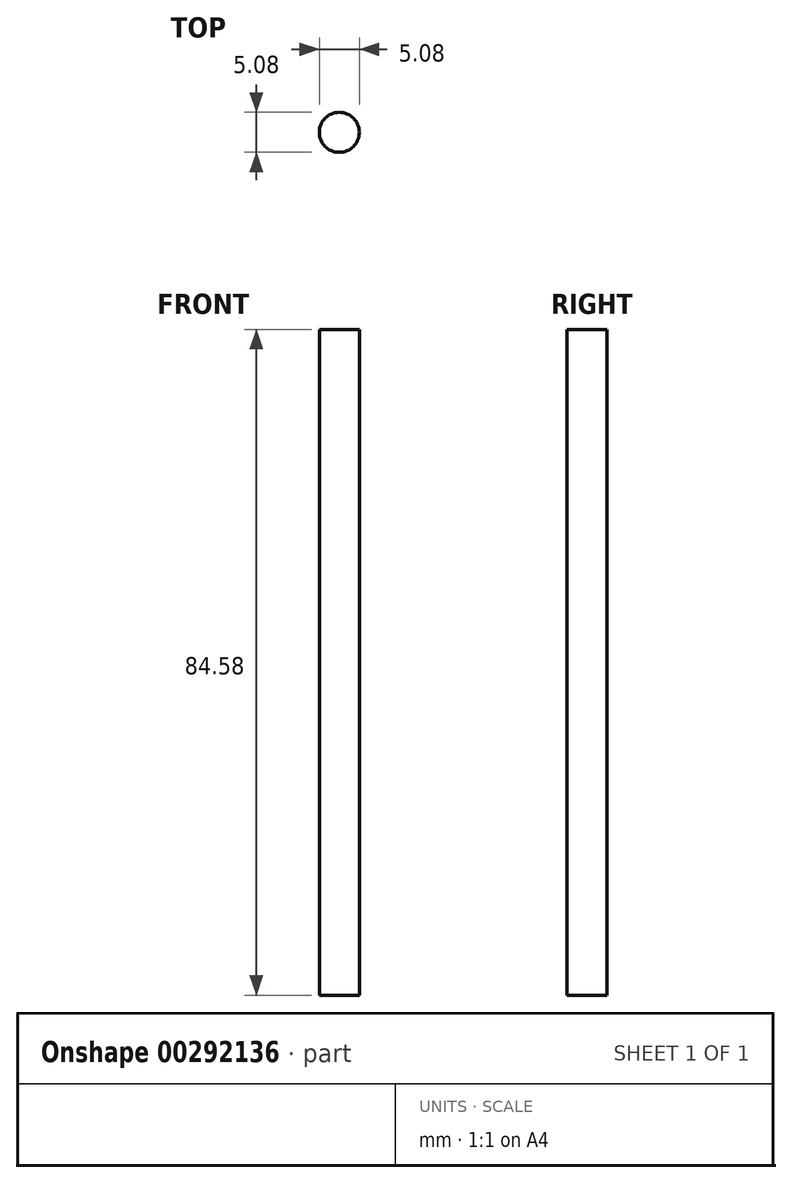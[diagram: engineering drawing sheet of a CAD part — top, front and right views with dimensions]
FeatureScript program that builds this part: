
annotation { "Feature Type Name" : "Feature", "Feature Type Description" : "" }
export const myFeature = defineFeature(function(context is Context, id is Id, definition is map)
    precondition{}
    {
        {
            var Q0;
            Q0=qCreatedBy(makeId("Front.planeOp"),FACE);
            var sketch = newSketch(context, id + "F0", { "sketchPlane" : qUnion([Q0])});
            skLineSegment(sketch, "E0.bottom", {"start": v(-2.54, 70.26) * mm, "end": v(0, 70.26) * mm});
            skLineSegment(sketch, "E0.top", {"start": v(-2.54, -14.32) * mm, "end": v(0, -14.32) * mm});
            skLineSegment(sketch, "E0.left", {"start": v(-2.54, 70.26) * mm, "end": v(-2.54, -14.32) * mm});
            skLineSegment(sketch, "E0.right", {"start": v(0, 70.26) * mm, "end": v(0, -14.32) * mm});
            skSolve(sketch);
        }
        {
            var Q0;
            Q0 = qSketchRegion(id + "F0", true);
            var Q1;
            Q1=sQuery(id+"F0.wireOp",EDGE,"E0.left");
            revolve(context, id + "F1", {"entities" : qUnion([Q0]), "axis" : qUnion([Q1]), "revolveType" : RevolveType.FULL});
        }
    });
